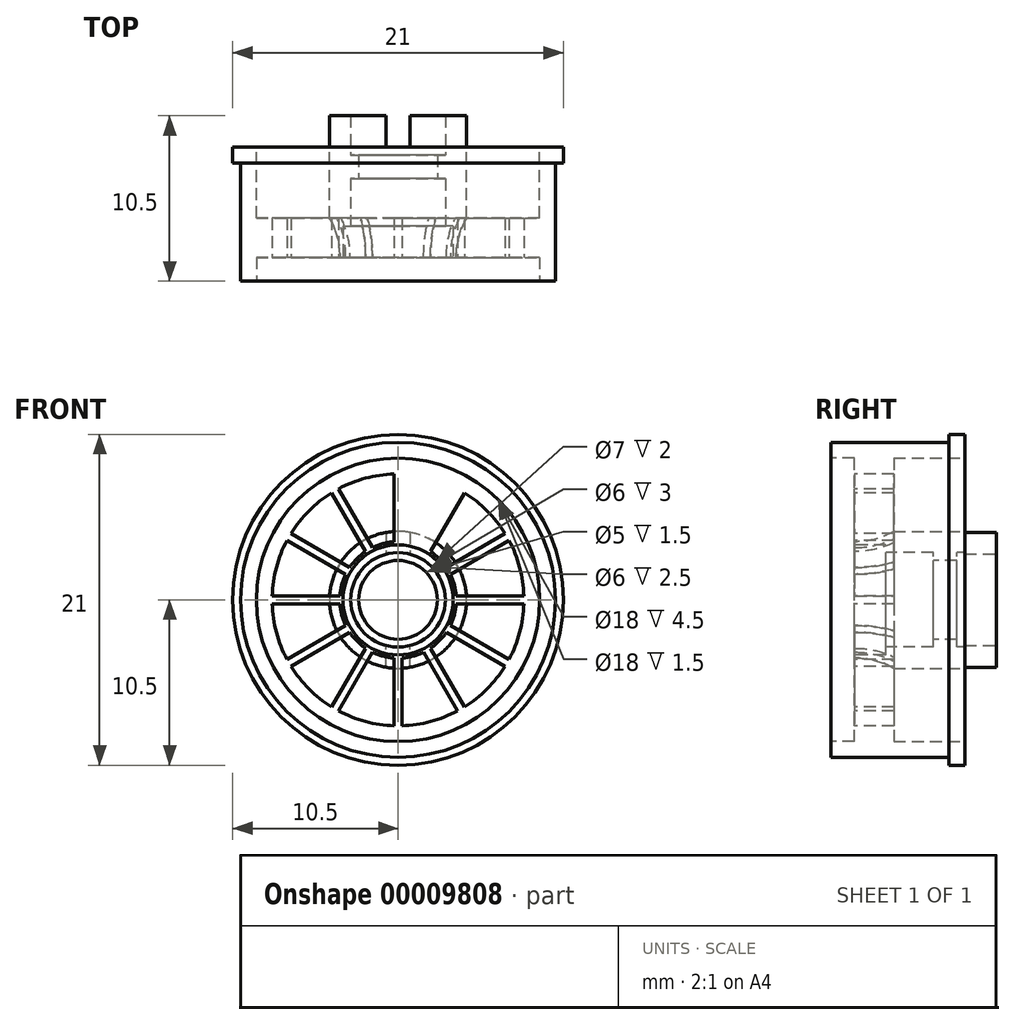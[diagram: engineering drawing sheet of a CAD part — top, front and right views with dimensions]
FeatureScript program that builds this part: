
annotation { "Feature Type Name" : "Feature", "Feature Type Description" : "" }
export const myFeature = defineFeature(function(context is Context, id is Id, definition is map)
    precondition{}
    {
        {
            var Q0;
            Q0=qCreatedBy(makeId("Front.planeOp"),FACE);
            var sketch = newSketch(context, id + "F0", { "sketchPlane" : qUnion([Q0])});
            skCircle(sketch, "E0", {"center": v(0, 0) * mm, "radius": 10.5 * mm});
            skSolve(sketch);
        }
        {
            var Q0;
            Q0=makeQuery(id+"F0.imprint","IMPRINT",FACE,{"disambiguationData":[TD([[makeQuery(id+"F0.imprint","IMPRINT",EDGE,{"derivedFrom":sQuery(id+"F0.wireOp",EDGE,"E0")}),1.0]])]});
            extrude(context, id + "F1", {"entities" : qUnion([Q0]), "depth" : 1 * mm});
        }
        {
            var Q0;
            Q0=makeQuery(id+"F1.opExtrude","CAP_FACE",FACE,{"disambiguationData":[OSD([sQuery(id+"F0.wireOp",EDGE,"E0")])],"isStart":false});
            var sketch = newSketch(context, id + "F2", { "sketchPlane" : qUnion([Q0])});
            skCircle(sketch, "E1", {"center": v(0, 0) * mm, "radius": 10 * mm});
            skSolve(sketch);
        }
        {
            var Q0;
            Q0=makeQuery(id+"F2.imprint","IMPRINT",FACE,{"disambiguationData":[TD([[makeQuery(id+"F2.imprint","IMPRINT",EDGE,{"derivedFrom":sQuery(id+"F2.wireOp",EDGE,"E1")}),1.0]])]});
            extrude(context, id + "F3", {"entities" : qUnion([Q0]), "operationType" : NewBodyOperationType.ADD, "depth" : 7.5 * mm});
        }
        {
            var Q0;
            Q0=makeQuery(id+"F3.opExtrude","CAP_FACE",FACE,{"disambiguationData":[OSD([sQuery(id+"F2.wireOp",EDGE,"E1")])],"isStart":false});
            var sketch = newSketch(context, id + "F4", { "sketchPlane" : qUnion([Q0])});
            skCircle(sketch, "E2", {"center": v(0, 0) * mm, "radius": 3.5 * mm});
            skSolve(sketch);
        }
        {
            var Q0;
            Q0=makeQuery(id+"F4.imprint","IMPRINT",FACE,{"disambiguationData":[TD([[makeQuery(id+"F4.imprint","IMPRINT",EDGE,{"derivedFrom":sQuery(id+"F4.wireOp",EDGE,"E2")}),1.0]])]});
            extrude(context, id + "F5", {"entities" : qUnion([Q0]), "operationType" : NewBodyOperationType.REMOVE, "oppositeDirection" : true, "depth" : 3.5 * mm});
        }
        {
            var Q0;
            Q0=makeQuery(id+"F5.boolean.opBoolean","COPY",FACE,{"derivedFrom":makeQuery(id+"F5.opExtrude","CAP_FACE",FACE,{"disambiguationData":[OSD([sQuery(id+"F4.wireOp",EDGE,"E2")])],"isStart":false})});
            var sketch = newSketch(context, id + "F6", { "sketchPlane" : qUnion([Q0])});
            skCircle(sketch, "E3", {"center": v(0, 0) * mm, "radius": 3 * mm});
            skSolve(sketch);
        }
        {
            var Q0;
            Q0=makeQuery(id+"F6.imprint","IMPRINT",FACE,{"disambiguationData":[TD([[makeQuery(id+"F6.imprint","IMPRINT",EDGE,{"derivedFrom":sQuery(id+"F6.wireOp",EDGE,"E3")}),1.0]])]});
            extrude(context, id + "F7", {"entities" : qUnion([Q0]), "operationType" : NewBodyOperationType.REMOVE, "oppositeDirection" : true, "depth" : 3 * mm});
        }
        {
            var Q0;
            Q0=makeQuery(id+"F7.boolean.opBoolean","COPY",FACE,{"derivedFrom":makeQuery(id+"F7.opExtrude","CAP_FACE",FACE,{"disambiguationData":[OSD([sQuery(id+"F6.wireOp",EDGE,"E3")])],"isStart":false})});
            var sketch = newSketch(context, id + "F8", { "sketchPlane" : qUnion([Q0])});
            skCircle(sketch, "E4", {"center": v(0, 0) * mm, "radius": 2.5 * mm});
            skSolve(sketch);
        }
        {
            var Q0;
            Q0=makeQuery(id+"F8.imprint","IMPRINT",FACE,{"disambiguationData":[TD([[makeQuery(id+"F8.imprint","IMPRINT",EDGE,{"derivedFrom":sQuery(id+"F8.wireOp",EDGE,"E4")}),1.0]])]});
            extrude(context, id + "F9", {"entities" : qUnion([Q0]), "operationType" : NewBodyOperationType.REMOVE, "oppositeDirection" : true, "depth" : 1.5 * mm});
        }
        {
            var Q0;
            Q0=makeQuery(id+"F9.boolean.opBoolean","COPY",FACE,{"derivedFrom":makeQuery(id+"F9.opExtrude","CAP_FACE",FACE,{"disambiguationData":[OSD([sQuery(id+"F8.wireOp",EDGE,"E4")])],"isStart":false})});
            var sketch = newSketch(context, id + "F10", { "sketchPlane" : qUnion([Q0])});
            skCircle(sketch, "E5", {"center": v(0, 0) * mm, "radius": 3 * mm});
            skSolve(sketch);
        }
        {
            var Q0;
            Q0 = qSketchRegion(id + "F10", true);
            extrude(context, id + "F11", {"entities" : qUnion([Q0]), "operationType" : NewBodyOperationType.REMOVE, "oppositeDirection" : true, "depth" : 25 * mm});
        }
        {
            var Q0;
            Q0=makeQuery(id+"F3.opExtrude","CAP_FACE",FACE,{"disambiguationData":[OSD([sQuery(id+"F2.wireOp",EDGE,"E1")])],"isStart":false});
            var sketch = newSketch(context, id + "F12", { "sketchPlane" : qUnion([Q0])});
            skCircle(sketch, "E6", {"center": v(0, 0) * mm, "radius": 9 * mm});
            skSolve(sketch);
        }
        {
            var Q0;
            Q0=makeQuery(id+"F1.opExtrude","CAP_FACE",FACE,{"disambiguationData":[OSD([sQuery(id+"F0.wireOp",EDGE,"E0")])],"isStart":true});
            var sketch = newSketch(context, id + "F13", { "sketchPlane" : qUnion([Q0])});
            skCircle(sketch, "E7", {"center": v(0, 0) * mm, "radius": 9 * mm});
            skCircle(sketch, "E8", {"center": v(0, 0) * mm, "radius": 4.35 * mm});
            skSolve(sketch);
        }
        {
            var Q0;
            Q0=makeQuery(id+"F13.imprint","IMPRINT",FACE,{"disambiguationData":[TD([[makeQuery(id+"F13.imprint","IMPRINT",EDGE,{"derivedFrom":sQuery(id+"F13.wireOp",EDGE,"E7")}),1.0]])]});
            extrude(context, id + "F14", {"entities" : qUnion([Q0]), "operationType" : NewBodyOperationType.REMOVE, "oppositeDirection" : true, "depth" : 4.5 * mm});
        }
        {
            var Q0;
            Q0=makeQuery(id+"F12.imprint","IMPRINT",FACE,{"disambiguationData":[TD([[makeQuery(id+"F12.imprint","IMPRINT",EDGE,{"derivedFrom":sQuery(id+"F12.wireOp",EDGE,"E6")}),1.0]])]});
            extrude(context, id + "F15", {"entities" : qUnion([Q0]), "operationType" : NewBodyOperationType.REMOVE, "oppositeDirection" : true, "depth" : 1.5 * mm});
        }
        {
            var Q0;
            Q0=makeQuery(id+"F15.boolean.opBoolean","COPY",FACE,{"derivedFrom":makeQuery(id+"F15.opExtrude","CAP_FACE",FACE,{"disambiguationData":[OSD([sQuery(id+"F4.wireOp",EDGE,"E2"),sQuery(id+"F12.wireOp",EDGE,"E6")])],"isStart":false})});
            var sketch = newSketch(context, id + "F16", { "sketchPlane" : qUnion([Q0])});
            skCircle(sketch, "E9.0", {"center": v(0, 0) * mm, "radius": 8 * mm});
            skCircle(sketch, "E10.0", {"center": v(0, 0) * mm, "radius": 3.7 * mm});
            skLineSegment(sketch, "E11", {"start": v(-1.85, 3.2) * mm, "end": v(-4, 6.93) * mm});
            skLineSegment(sketch, "E12", {"start": v(0, 3.7) * mm, "end": v(0, 8) * mm});
            skLineSegment(sketch, "E13", {"start": v(-0.25, 3.7) * mm, "end": v(-0.25, 8) * mm});
            skLineSegment(sketch, "E14.0.MirrorCS", {"start": v(0.25, 3.7) * mm, "end": v(0.25, 8) * mm});
            skLineSegment(sketch, "E15", {"start": v(-2.06, 3.07) * mm, "end": v(-4.21, 6.8) * mm});
            skLineSegment(sketch, "E16.0.MirrorCS", {"start": v(-1.63, 3.32) * mm, "end": v(-3.78, 7.05) * mm});
            skLineSegment(sketch, "E17.1.0", {"start": v(-3.07, 2.06) * mm, "end": v(-6.8, 4.21) * mm});
            skLineSegment(sketch, "E17.2.0", {"start": v(-3.7, 0.25) * mm, "end": v(-8, 0.25) * mm});
            skLineSegment(sketch, "E17.2.1", {"start": v(-3.32, 1.63) * mm, "end": v(-7.05, 3.78) * mm});
            skLineSegment(sketch, "E17.3.0", {"start": v(-3.32, -1.63) * mm, "end": v(-7.05, -3.78) * mm});
            skLineSegment(sketch, "E17.3.1", {"start": v(-3.7, -0.25) * mm, "end": v(-8, -0.25) * mm});
            skLineSegment(sketch, "E17.4.0", {"start": v(-2.06, -3.07) * mm, "end": v(-4.21, -6.8) * mm});
            skLineSegment(sketch, "E17.4.1", {"start": v(-3.07, -2.06) * mm, "end": v(-6.8, -4.21) * mm});
            skLineSegment(sketch, "E17.5.0", {"start": v(-0.25, -3.7) * mm, "end": v(-0.25, -8) * mm});
            skLineSegment(sketch, "E17.5.1", {"start": v(-1.63, -3.32) * mm, "end": v(-3.78, -7.05) * mm});
            skLineSegment(sketch, "E17.6.0", {"start": v(1.63, -3.32) * mm, "end": v(3.78, -7.05) * mm});
            skLineSegment(sketch, "E17.6.1", {"start": v(0.25, -3.7) * mm, "end": v(0.25, -8) * mm});
            skLineSegment(sketch, "E17.7.0", {"start": v(3.07, -2.06) * mm, "end": v(6.8, -4.21) * mm});
            skLineSegment(sketch, "E17.7.1", {"start": v(2.06, -3.07) * mm, "end": v(4.21, -6.8) * mm});
            skLineSegment(sketch, "E17.8.0", {"start": v(3.7, -0.25) * mm, "end": v(8, -0.25) * mm});
            skLineSegment(sketch, "E17.8.1", {"start": v(3.32, -1.63) * mm, "end": v(7.05, -3.78) * mm});
            skLineSegment(sketch, "E17.9.0", {"start": v(3.32, 1.63) * mm, "end": v(7.05, 3.78) * mm});
            skLineSegment(sketch, "E17.9.1", {"start": v(3.7, 0.25) * mm, "end": v(8, 0.25) * mm});
            skLineSegment(sketch, "E17.10.0", {"start": v(2.06, 3.07) * mm, "end": v(4.21, 6.8) * mm});
            skLineSegment(sketch, "E17.10.1", {"start": v(3.07, 2.06) * mm, "end": v(6.8, 4.21) * mm});
            skLineSegment(sketch, "E17.11.1", {"start": v(1.63, 3.32) * mm, "end": v(3.78, 7.05) * mm});
            skSolve(sketch);
        }
        {
            var Q0;
            {var subQ1=sQuery(id+"F16.wireOp",EDGE,"E13");Q0=makeQuery(id+"F16.imprint","IMPRINT",FACE,{"disambiguationData":[TD([[makeQuery(id+"F16.imprint","IMPRINT",EDGE,{"derivedFrom":subQ1}),1.0]])]});}
            var Q1;
            {var subQ1=sQuery(id+"F16.wireOp",EDGE,"E14.0.MirrorCS");Q1=makeQuery(id+"F16.imprint","IMPRINT",FACE,{"disambiguationData":[TD([[makeQuery(id+"F16.imprint","IMPRINT",EDGE,{"derivedFrom":subQ1}),-1.0]])]});}
            var Q2;
            {var subQ1=sQuery(id+"F16.wireOp",EDGE,"E17.10.0");Q2=makeQuery(id+"F16.imprint","IMPRINT",FACE,{"disambiguationData":[TD([[makeQuery(id+"F16.imprint","IMPRINT",EDGE,{"derivedFrom":subQ1}),-1.0]])]});}
            var Q3;
            {var subQ1=sQuery(id+"F16.wireOp",EDGE,"E17.9.0");Q3=makeQuery(id+"F16.imprint","IMPRINT",FACE,{"disambiguationData":[TD([[makeQuery(id+"F16.imprint","IMPRINT",EDGE,{"derivedFrom":subQ1}),-1.0]])]});}
            var Q4;
            {var subQ1=sQuery(id+"F16.wireOp",EDGE,"E17.8.0");Q4=makeQuery(id+"F16.imprint","IMPRINT",FACE,{"disambiguationData":[TD([[makeQuery(id+"F16.imprint","IMPRINT",EDGE,{"derivedFrom":subQ1}),-1.0]])]});}
            var Q5;
            {var subQ1=sQuery(id+"F16.wireOp",EDGE,"E17.7.0");Q5=makeQuery(id+"F16.imprint","IMPRINT",FACE,{"disambiguationData":[TD([[makeQuery(id+"F16.imprint","IMPRINT",EDGE,{"derivedFrom":subQ1}),-1.0]])]});}
            var Q6;
            {var subQ2=sQuery(id+"F16.wireOp",EDGE,"E17.1.0");Q6=makeQuery(id+"F16.imprint","IMPRINT",FACE,{"disambiguationData":[TD([[makeQuery(id+"F16.imprint","IMPRINT",EDGE,{"derivedFrom":subQ2}),-1.0]])]});}
            var Q7;
            {var subQ2=sQuery(id+"F16.wireOp",EDGE,"E17.2.0");Q7=makeQuery(id+"F16.imprint","IMPRINT",FACE,{"disambiguationData":[TD([[makeQuery(id+"F16.imprint","IMPRINT",EDGE,{"derivedFrom":subQ2}),-1.0]])]});}
            var Q8;
            {var subQ2=sQuery(id+"F16.wireOp",EDGE,"E17.3.0");Q8=makeQuery(id+"F16.imprint","IMPRINT",FACE,{"disambiguationData":[TD([[makeQuery(id+"F16.imprint","IMPRINT",EDGE,{"derivedFrom":subQ2}),-1.0]])]});}
            var Q9;
            {var subQ1=sQuery(id+"F16.wireOp",EDGE,"E17.4.0");Q9=makeQuery(id+"F16.imprint","IMPRINT",FACE,{"disambiguationData":[TD([[makeQuery(id+"F16.imprint","IMPRINT",EDGE,{"derivedFrom":subQ1}),-1.0]])]});}
            var Q10;
            {var subQ1=sQuery(id+"F16.wireOp",EDGE,"E17.5.0");Q10=makeQuery(id+"F16.imprint","IMPRINT",FACE,{"disambiguationData":[TD([[makeQuery(id+"F16.imprint","IMPRINT",EDGE,{"derivedFrom":subQ1}),-1.0]])]});}
            var Q11;
            {var subQ1=sQuery(id+"F16.wireOp",EDGE,"E17.6.0");Q11=makeQuery(id+"F16.imprint","IMPRINT",FACE,{"disambiguationData":[TD([[makeQuery(id+"F16.imprint","IMPRINT",EDGE,{"derivedFrom":subQ1}),-1.0]])]});}
            extrude(context, id + "F17", {"entities" : qUnion([Q0, Q1, Q2, Q3, Q4, Q5, Q6, Q7, Q8, Q9, Q10, Q11]), "operationType" : NewBodyOperationType.REMOVE, "oppositeDirection" : true, "depth" : 2.5 * mm});
        }
        {
            var Q0;
            {var subQ0=sQuery(id+"F16.wireOp",EDGE,"E10.0");Q0=makeQuery(id+"F17.boolean.opBoolean","COPY",EDGE,{"derivedFrom":makeQuery(id+"F17.opExtrude","CAP_EDGE",EDGE,{"disambiguationData":[OSD([subQ0]),TDD([makeQuery(id+"F16.imprint","IMPRINT",EDGE,{"disambiguationData":[TD([[makeQuery(id+"F16.imprint","INTERSECT",VERTEX,{"derivedFrom":[subQ0,sQuery(id+"F16.wireOp",EDGE,"E17.1.0")]}),1.0]])],"derivedFrom":subQ0})])],"isStart":false})});}
            var Q1;
            {var subQ0=sQuery(id+"F16.wireOp",EDGE,"E10.0");Q1=makeQuery(id+"F17.boolean.opBoolean","COPY",EDGE,{"derivedFrom":makeQuery(id+"F17.opExtrude","CAP_EDGE",EDGE,{"disambiguationData":[OSD([subQ0]),TDD([makeQuery(id+"F16.imprint","IMPRINT",EDGE,{"disambiguationData":[TD([[makeQuery(id+"F16.imprint","INTERSECT",VERTEX,{"derivedFrom":[subQ0,sQuery(id+"F16.wireOp",EDGE,"E13")]}),-1.0]])],"derivedFrom":subQ0})])],"isStart":false})});}
            var Q2;
            {var subQ0=sQuery(id+"F16.wireOp",EDGE,"E10.0");Q2=makeQuery(id+"F17.boolean.opBoolean","COPY",EDGE,{"derivedFrom":makeQuery(id+"F17.opExtrude","CAP_EDGE",EDGE,{"disambiguationData":[OSD([subQ0]),TDD([makeQuery(id+"F16.imprint","IMPRINT",EDGE,{"disambiguationData":[TD([[makeQuery(id+"F16.imprint","INTERSECT",VERTEX,{"derivedFrom":[subQ0,sQuery(id+"F16.wireOp",EDGE,"E14.0.MirrorCS")]}),1.0]])],"derivedFrom":subQ0})])],"isStart":false})});}
            var Q3;
            {var subQ0=sQuery(id+"F16.wireOp",EDGE,"E10.0");Q3=makeQuery(id+"F17.boolean.opBoolean","COPY",EDGE,{"derivedFrom":makeQuery(id+"F17.opExtrude","CAP_EDGE",EDGE,{"disambiguationData":[OSD([subQ0]),TDD([makeQuery(id+"F16.imprint","IMPRINT",EDGE,{"disambiguationData":[TD([[makeQuery(id+"F16.imprint","INTERSECT",VERTEX,{"derivedFrom":[subQ0,sQuery(id+"F16.wireOp",EDGE,"E17.10.0")]}),1.0]])],"derivedFrom":subQ0})])],"isStart":false})});}
            var Q4;
            {var subQ0=sQuery(id+"F16.wireOp",EDGE,"E10.0");Q4=makeQuery(id+"F17.boolean.opBoolean","COPY",EDGE,{"derivedFrom":makeQuery(id+"F17.opExtrude","CAP_EDGE",EDGE,{"disambiguationData":[OSD([subQ0]),TDD([makeQuery(id+"F16.imprint","IMPRINT",EDGE,{"disambiguationData":[TD([[makeQuery(id+"F16.imprint","INTERSECT",VERTEX,{"derivedFrom":[subQ0,sQuery(id+"F16.wireOp",EDGE,"E17.2.0")]}),1.0]])],"derivedFrom":subQ0})])],"isStart":false})});}
            var Q5;
            {var subQ0=sQuery(id+"F16.wireOp",EDGE,"E10.0");Q5=makeQuery(id+"F17.boolean.opBoolean","COPY",EDGE,{"derivedFrom":makeQuery(id+"F17.opExtrude","CAP_EDGE",EDGE,{"disambiguationData":[OSD([subQ0]),TDD([makeQuery(id+"F16.imprint","IMPRINT",EDGE,{"disambiguationData":[TD([[makeQuery(id+"F16.imprint","INTERSECT",VERTEX,{"derivedFrom":[subQ0,sQuery(id+"F16.wireOp",EDGE,"E17.3.0")]}),1.0]])],"derivedFrom":subQ0})])],"isStart":false})});}
            var Q6;
            {var subQ0=sQuery(id+"F16.wireOp",EDGE,"E10.0");Q6=makeQuery(id+"F17.boolean.opBoolean","COPY",EDGE,{"derivedFrom":makeQuery(id+"F17.opExtrude","CAP_EDGE",EDGE,{"disambiguationData":[OSD([subQ0]),TDD([makeQuery(id+"F16.imprint","IMPRINT",EDGE,{"disambiguationData":[TD([[makeQuery(id+"F16.imprint","INTERSECT",VERTEX,{"derivedFrom":[subQ0,sQuery(id+"F16.wireOp",EDGE,"E17.9.0")]}),1.0]])],"derivedFrom":subQ0})])],"isStart":false})});}
            var Q7;
            {var subQ0=sQuery(id+"F16.wireOp",EDGE,"E10.0");Q7=makeQuery(id+"F17.boolean.opBoolean","COPY",EDGE,{"derivedFrom":makeQuery(id+"F17.opExtrude","CAP_EDGE",EDGE,{"disambiguationData":[OSD([subQ0]),TDD([makeQuery(id+"F16.imprint","IMPRINT",EDGE,{"disambiguationData":[TD([[makeQuery(id+"F16.imprint","INTERSECT",VERTEX,{"derivedFrom":[subQ0,sQuery(id+"F16.wireOp",EDGE,"E17.8.0")]}),1.0]])],"derivedFrom":subQ0})])],"isStart":false})});}
            var Q8;
            {var subQ0=sQuery(id+"F16.wireOp",EDGE,"E10.0");Q8=makeQuery(id+"F17.boolean.opBoolean","COPY",EDGE,{"derivedFrom":makeQuery(id+"F17.opExtrude","CAP_EDGE",EDGE,{"disambiguationData":[OSD([subQ0]),TDD([makeQuery(id+"F16.imprint","IMPRINT",EDGE,{"disambiguationData":[TD([[makeQuery(id+"F16.imprint","INTERSECT",VERTEX,{"derivedFrom":[subQ0,sQuery(id+"F16.wireOp",EDGE,"E17.7.0")]}),1.0]])],"derivedFrom":subQ0})])],"isStart":false})});}
            var Q9;
            {var subQ0=sQuery(id+"F16.wireOp",EDGE,"E10.0");Q9=makeQuery(id+"F17.boolean.opBoolean","COPY",EDGE,{"derivedFrom":makeQuery(id+"F17.opExtrude","CAP_EDGE",EDGE,{"disambiguationData":[OSD([subQ0]),TDD([makeQuery(id+"F16.imprint","IMPRINT",EDGE,{"disambiguationData":[TD([[makeQuery(id+"F16.imprint","INTERSECT",VERTEX,{"derivedFrom":[subQ0,sQuery(id+"F16.wireOp",EDGE,"E17.6.0")]}),1.0]])],"derivedFrom":subQ0})])],"isStart":false})});}
            var Q10;
            {var subQ0=sQuery(id+"F16.wireOp",EDGE,"E10.0");Q10=makeQuery(id+"F17.boolean.opBoolean","COPY",EDGE,{"derivedFrom":makeQuery(id+"F17.opExtrude","CAP_EDGE",EDGE,{"disambiguationData":[OSD([subQ0]),TDD([makeQuery(id+"F16.imprint","IMPRINT",EDGE,{"disambiguationData":[TD([[makeQuery(id+"F16.imprint","INTERSECT",VERTEX,{"derivedFrom":[subQ0,sQuery(id+"F16.wireOp",EDGE,"E17.5.0")]}),1.0]])],"derivedFrom":subQ0})])],"isStart":false})});}
            var Q11;
            {var subQ0=sQuery(id+"F16.wireOp",EDGE,"E10.0");Q11=makeQuery(id+"F17.boolean.opBoolean","COPY",EDGE,{"derivedFrom":makeQuery(id+"F17.opExtrude","CAP_EDGE",EDGE,{"disambiguationData":[OSD([subQ0]),TDD([makeQuery(id+"F16.imprint","IMPRINT",EDGE,{"disambiguationData":[TD([[makeQuery(id+"F16.imprint","INTERSECT",VERTEX,{"derivedFrom":[subQ0,sQuery(id+"F16.wireOp",EDGE,"E17.4.0")]}),1.0]])],"derivedFrom":subQ0})])],"isStart":false})});}
            fillet(context, id + "F18", {"entities" : qUnion([Q0, Q1, Q2, Q3, Q4, Q5, Q6, Q7, Q8, Q9, Q10, Q11]), "radius" : 5 * mm, "tangentPropagation" : true, "allowEdgeOverflow" : false});
        }
        {
            var Q0;
            Q0=makeQuery(id+"F14.boolean.opBoolean","SPLIT",FACE,{"disambiguationData":[TD([makeQuery(id+"F11.boolean.opBoolean","COPY",FACE,{"derivedFrom":makeQuery(id+"F11.opExtrude","SWEPT_FACE",FACE,{"disambiguationData":[OSD([sQuery(id+"F10.wireOp",EDGE,"E5")])]})})])],"derivedFrom":makeQuery(id+"F1.opExtrude","CAP_FACE",FACE,{"disambiguationData":[OSD([sQuery(id+"F0.wireOp",EDGE,"E0")])],"isStart":true})});
            extrude(context, id + "F19", {"entities" : qUnion([Q0]), "operationType" : NewBodyOperationType.ADD, "depth" : 2 * mm});
        }
        {
            var Q0;
            Q0=makeQuery(id+"F19.opExtrude","CAP_FACE",FACE,{"disambiguationData":[OSD([sQuery(id+"F0.wireOp",EDGE,"E0")])],"isStart":false});
            var sketch = newSketch(context, id + "F20", { "sketchPlane" : qUnion([Q0])});
            skLineSegment(sketch, "E18", {"start": v(0, 3) * mm, "end": v(0, 4.35) * mm});
            skLineSegment(sketch, "E19", {"start": v(-0.75, 4.28) * mm, "end": v(-0.75, 2.9) * mm});
            skLineSegment(sketch, "E20.0.MirrorCS", {"start": v(0.75, 4.28) * mm, "end": v(0.75, 2.9) * mm});
            skLineSegment(sketch, "E21", {"start": v(0, 0) * mm, "end": v(2.07, 0) * mm});
            skLineSegment(sketch, "E22.0.MirrorCS", {"start": v(-0.75, -4.28) * mm, "end": v(-0.75, -2.9) * mm});
            skLineSegment(sketch, "E23.0.MirrorCS", {"start": v(0.75, -4.28) * mm, "end": v(0.75, -2.9) * mm});
            skSolve(sketch);
        }
        {
            var Q0;
            {var subQ2=sQuery(id+"F20.wireOp",EDGE,"E18");Q0=makeQuery(id+"F20.imprint","IMPRINT",FACE,{"disambiguationData":[TD([[makeQuery(id+"F20.imprint","IMPRINT",EDGE,{"derivedFrom":subQ2}),1.0]])]});}
            var Q1;
            {var subQ2=sQuery(id+"F20.wireOp",EDGE,"E18");Q1=makeQuery(id+"F20.imprint","IMPRINT",FACE,{"disambiguationData":[TD([[makeQuery(id+"F20.imprint","IMPRINT",EDGE,{"derivedFrom":subQ2}),-1.0]])]});}
            var Q2;
            {var subQ2=sQuery(id+"F20.wireOp",EDGE,"E22.0.MirrorCS");Q2=makeQuery(id+"F20.imprint","IMPRINT",FACE,{"disambiguationData":[TD([[makeQuery(id+"F20.imprint","IMPRINT",EDGE,{"derivedFrom":subQ2}),-1.0]])]});}
            extrude(context, id + "F21", {"entities" : qUnion([Q0, Q1, Q2]), "operationType" : NewBodyOperationType.REMOVE, "oppositeDirection" : true, "depth" : 2 * mm});
        }
    });
